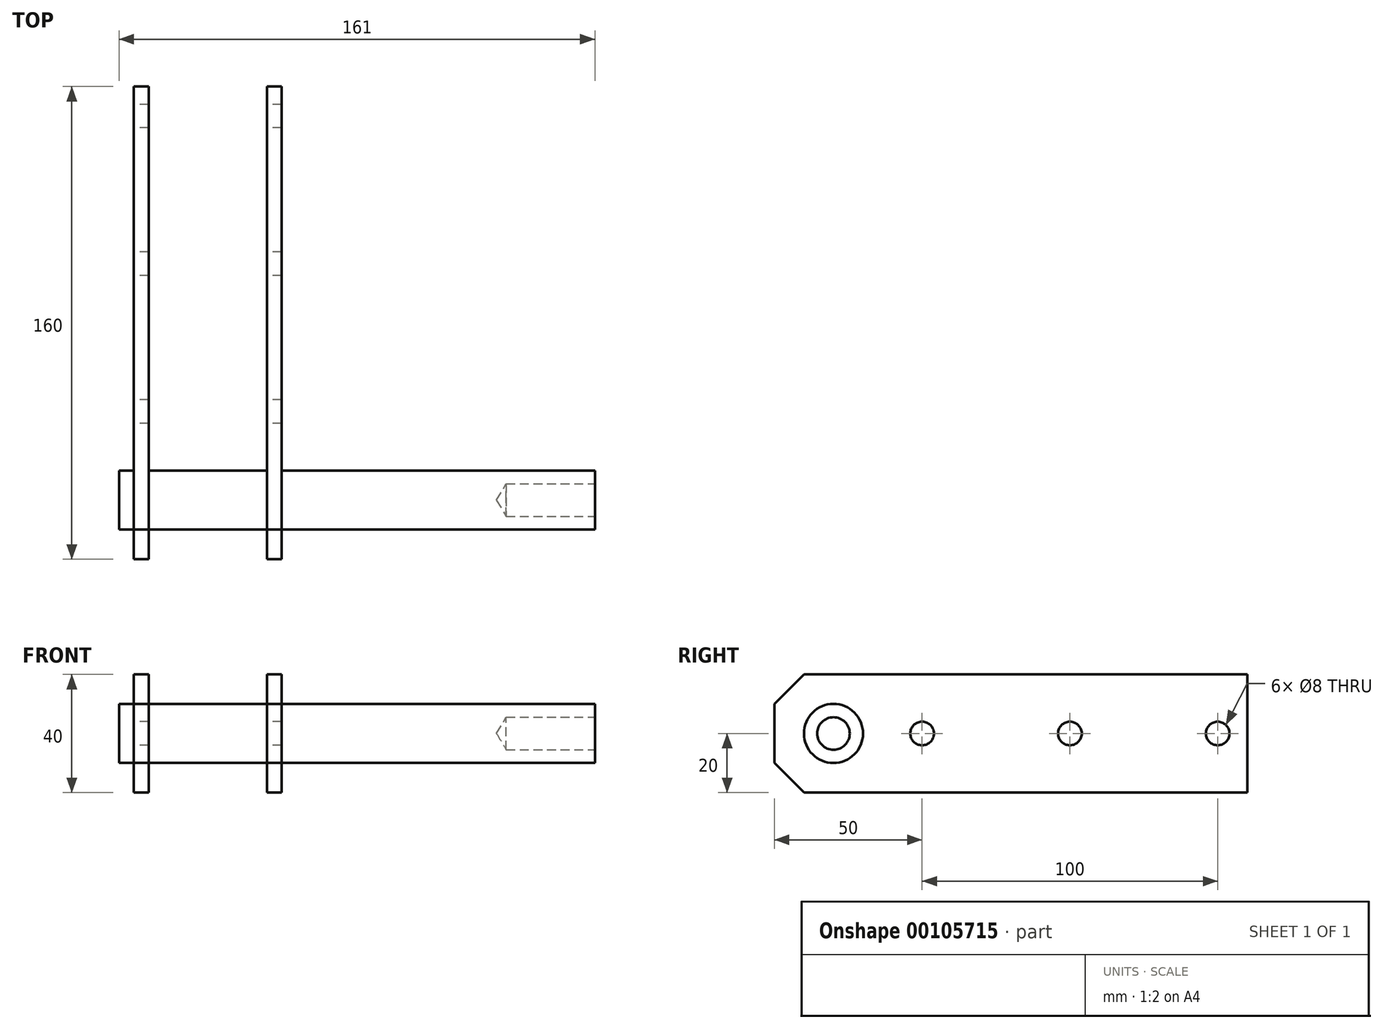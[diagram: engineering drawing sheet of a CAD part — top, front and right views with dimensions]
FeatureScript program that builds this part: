
annotation { "Feature Type Name" : "Feature", "Feature Type Description" : "" }
export const myFeature = defineFeature(function(context is Context, id is Id, definition is map)
    precondition{}
    {
        {
            var Q0;
            Q0=qCreatedBy(makeId("Right.planeOp"),FACE);
            var sketch = newSketch(context, id + "F0", { "sketchPlane" : qUnion([Q0])});
            skCircle(sketch, "E0", {"center": v(0, 0) * mm, "radius": 10 * mm});
            skSolve(sketch);
        }
        {
            var Q0;
            Q0=makeQuery(id+"F0.imprint","IMPRINT",FACE,{"disambiguationData":[TD([[makeQuery(id+"F0.imprint","IMPRINT",EDGE,{"derivedFrom":sQuery(id+"F0.wireOp",EDGE,"E0")}),1.0]])]});
            extrude(context, id + "F1", {"entities" : qUnion([Q0]), "depth" : 161 * mm});
        }
        {
            var Q0;
            Q0=qCreatedBy(makeId("Right.planeOp"),FACE);
            cPlane(context, id + "F2", {"entities" : qUnion([Q0]), "cplaneType" : CPlaneType.OFFSET, "offset" : 5 * mm, "width" : 150 * mm, "height" : 150 * mm});
        }
        {
            var Q0;
            Q0=qCreatedBy(id+"F2.planeOp",FACE);
            var sketch = newSketch(context, id + "F3", { "sketchPlane" : qUnion([Q0])});
            skLineSegment(sketch, "E1.bottom", {"start": v(140, 20) * mm, "end": v(-20, 20) * mm});
            skLineSegment(sketch, "E1.top", {"start": v(140, -20) * mm, "end": v(-20, -20) * mm});
            skLineSegment(sketch, "E1.left", {"start": v(140, 20) * mm, "end": v(140, -20) * mm});
            skLineSegment(sketch, "E1.right", {"start": v(-20, 20) * mm, "end": v(-20, -20) * mm});
            skSolve(sketch);
        }
        {
            var Q0;
            Q0=makeQuery(id+"F3.imprint","IMPRINT",FACE,{"disambiguationData":[TD([[makeQuery(id+"F3.imprint","IMPRINT",EDGE,{"derivedFrom":sQuery(id+"F3.wireOp",EDGE,"E1.bottom")}),1.0]])]});
            extrude(context, id + "F4", {"entities" : qUnion([Q0]), "operationType" : NewBodyOperationType.ADD, "depth" : 5 * mm});
        }
        {
            var Q0;
            Q0=makeQuery(id+"F4.opExtrude","CAP_FACE",FACE,{"disambiguationData":[OSD([sQuery(id+"F3.wireOp",EDGE,"E1.bottom"),sQuery(id+"F3.wireOp",EDGE,"E1.top"),sQuery(id+"F3.wireOp",EDGE,"E1.left"),sQuery(id+"F3.wireOp",EDGE,"E1.right")])],"isStart":false});
            cPlane(context, id + "F5", {"entities" : qUnion([Q0]), "cplaneType" : CPlaneType.OFFSET, "offset" : 40 * mm, "width" : 150 * mm, "height" : 150 * mm});
        }
        {
            var Q0;
            Q0=qCreatedBy(id+"F5.planeOp",FACE);
            var sketch = newSketch(context, id + "F6", { "sketchPlane" : qUnion([Q0])});
            skLineSegment(sketch, "E2.bottom", {"start": v(-20, 20) * mm, "end": v(140, 20) * mm});
            skLineSegment(sketch, "E2.top", {"start": v(-20, -20) * mm, "end": v(140, -20) * mm});
            skLineSegment(sketch, "E2.left", {"start": v(-20, 20) * mm, "end": v(-20, -20) * mm});
            skLineSegment(sketch, "E2.right", {"start": v(140, 20) * mm, "end": v(140, -20) * mm});
            skSolve(sketch);
        }
        {
            var Q0;
            Q0=makeQuery(id+"F6.imprint","IMPRINT",FACE,{"disambiguationData":[TD([[makeQuery(id+"F6.imprint","IMPRINT",EDGE,{"derivedFrom":sQuery(id+"F6.wireOp",EDGE,"E2.bottom")}),-1.0]])]});
            extrude(context, id + "F7", {"entities" : qUnion([Q0]), "operationType" : NewBodyOperationType.ADD, "depth" : 5 * mm});
        }
        {
            var Q0;
            Q0=makeQuery(id+"F7.opExtrude","SWEPT_EDGE",EDGE,{"disambiguationData":[OSD([sQuery(id+"F6.wireOp",EDGE,"E2.bottom"),sQuery(id+"F6.wireOp",EDGE,"E2.left")])]});
            var Q1;
            Q1=makeQuery(id+"F4.opExtrude","SWEPT_EDGE",EDGE,{"disambiguationData":[OSD([sQuery(id+"F3.wireOp",EDGE,"E1.bottom"),sQuery(id+"F3.wireOp",EDGE,"E1.right")])]});
            var Q2;
            Q2=makeQuery(id+"F4.opExtrude","SWEPT_EDGE",EDGE,{"disambiguationData":[OSD([sQuery(id+"F3.wireOp",EDGE,"E1.top"),sQuery(id+"F3.wireOp",EDGE,"E1.right")])]});
            var Q3;
            Q3=makeQuery(id+"F7.opExtrude","SWEPT_EDGE",EDGE,{"disambiguationData":[OSD([sQuery(id+"F6.wireOp",EDGE,"E2.top"),sQuery(id+"F6.wireOp",EDGE,"E2.left")])]});
            chamfer(context, id + "F8", {"entities" : qUnion([Q0, Q1, Q2, Q3]), "width" : 10 * mm, "tangentPropagation" : true});
        }
        {
            var Q0;
            Q0=makeQuery(id+"F4.opExtrude","CAP_FACE",FACE,{"disambiguationData":[OSD([sQuery(id+"F3.wireOp",EDGE,"E1.bottom"),sQuery(id+"F3.wireOp",EDGE,"E1.top"),sQuery(id+"F3.wireOp",EDGE,"E1.left"),sQuery(id+"F3.wireOp",EDGE,"E1.right")])],"isStart":true});
            var sketch = newSketch(context, id + "F9", { "sketchPlane" : qUnion([Q0])});
            skPoint(sketch, "E3", {"position": v(-130, 0) * mm});
            skPoint(sketch, "E4", {"position": v(-80, 0) * mm});
            skPoint(sketch, "E5", {"position": v(-30, 0) * mm});
            skPoint(sketch, "E6", {"position": v(-140, 0) * mm});
            skSolve(sketch);
        }
        {
            var Q0;
            Q0=sQuery(id+"F9.wireOp",VERTEX,"E3");
            var Q1;
            Q1=sQuery(id+"F9.wireOp",VERTEX,"E4");
            var Q2;
            Q2=sQuery(id+"F9.wireOp",VERTEX,"E5");
            var Q3;
            Q3=makeQuery(id+"F1.opExtrude","SWEPT_BODY",BODY,{"disambiguationData":[OSD([sQuery(id+"F0.wireOp",EDGE,"E0")])]});
            hole(context, id + "F10", {"style" : HoleStyle.SIMPLE, "endStyle" : HoleEndStyle.THROUGH, "holeDiameter" : 8 * mm, "locations" : qUnion([Q0, Q1, Q2]), "scope" : qUnion([Q3]), "isTappedThrough" : true});
        }
        {
            var Q0;
            Q0=makeQuery(id+"F1.opExtrude","CAP_FACE",FACE,{"disambiguationData":[OSD([sQuery(id+"F0.wireOp",EDGE,"E0")])],"isStart":false});
            var sketch = newSketch(context, id + "F11", { "sketchPlane" : qUnion([Q0])});
            skPoint(sketch, "E7", {"position": v(0, 0) * mm});
            skSolve(sketch);
        }
        {
            var Q0;
            Q0=sQuery(id+"F11.wireOp",VERTEX,"E7");
            var Q1;
            Q1=makeQuery(id+"F1.opExtrude","SWEPT_BODY",BODY,{"disambiguationData":[OSD([sQuery(id+"F0.wireOp",EDGE,"E0")])]});
            hole(context, id + "F12", {"style" : HoleStyle.SIMPLE, "endStyle" : HoleEndStyle.BLIND, "standardTappedOrClearance" : lookupTablePath({ "standard" : "ISO", "fit" : "Normal", "size" : "M10", "type" : "Clearance" }), "standardBlindInLast" : lookupTablePath({ "fit" : "Standard", "standard" : "ISO", "size" : "M10", "type" : "Clearance" }), "holeDiameter" : 11 * mm, "holeDepth" : 30 * mm, "locations" : qUnion([Q0]), "scope" : qUnion([Q1])});
        }
    });
